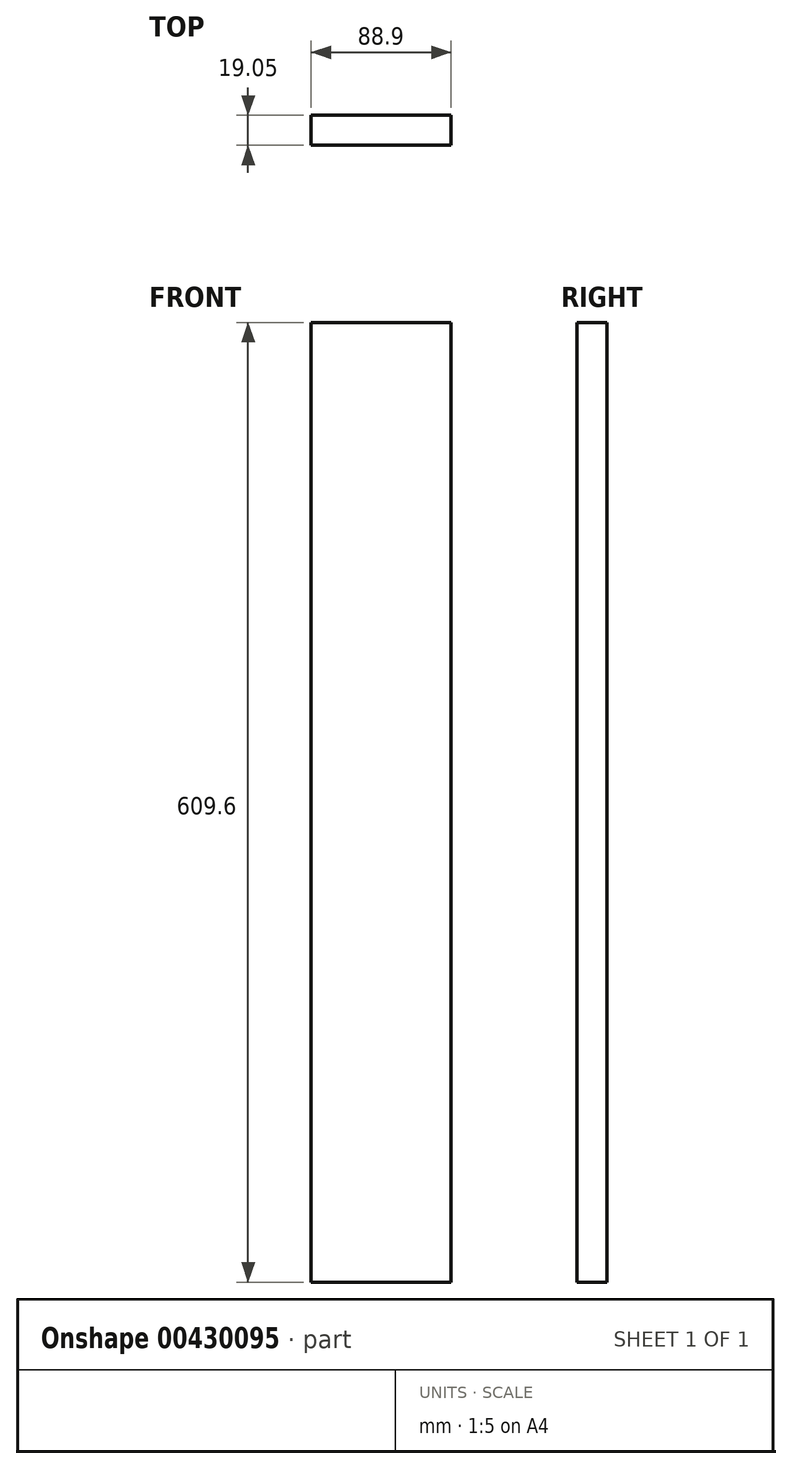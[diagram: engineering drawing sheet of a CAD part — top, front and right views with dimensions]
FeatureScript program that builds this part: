
annotation { "Feature Type Name" : "Feature", "Feature Type Description" : "" }
export const myFeature = defineFeature(function(context is Context, id is Id, definition is map)
    precondition{}
    {
        {
            var Q0;
            Q0=qCreatedBy(makeId("Top.planeOp"),FACE);
            var sketch = newSketch(context, id + "F0", { "sketchPlane" : qUnion([Q0])});
            skLineSegment(sketch, "E0.bottom", {"start": v(0, 0) * mm, "end": v(88.9, 0) * mm});
            skLineSegment(sketch, "E0.top", {"start": v(0, -19.05) * mm, "end": v(88.9, -19.05) * mm});
            skLineSegment(sketch, "E0.left", {"start": v(0, 0) * mm, "end": v(0, -19.05) * mm});
            skLineSegment(sketch, "E0.right", {"start": v(88.9, 0) * mm, "end": v(88.9, -19.05) * mm});
            skSolve(sketch);
        }
        {
            var Q0;
            Q0=makeQuery(id+"F0.imprint","IMPRINT",FACE,{"disambiguationData":[TD([[makeQuery(id+"F0.imprint","IMPRINT",EDGE,{"derivedFrom":sQuery(id+"F0.wireOp",EDGE,"E0.bottom")}),-1.0]])]});
            extrude(context, id + "F1", {"entities" : qUnion([Q0]), "depth" : 609.6 * mm});
        }
    });
